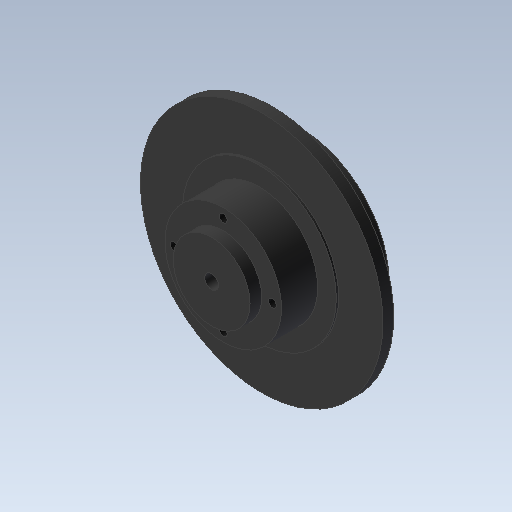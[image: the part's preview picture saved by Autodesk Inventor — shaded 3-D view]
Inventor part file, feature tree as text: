
AUTODESK INVENTOR PART (.ipt)
format: ipt  version: 2021 (Build 250183000, 183)  size: 157,696 bytes
history: native  units: mm
features: sketch x7, extrude x6, hole x1
ambient origin geometry x8: Origin, YZ Plane, XZ Plane, XY Plane, X Axis, Y Axis, Z Axis, Center Point
bodies: Solid1 (feature_tree)
feature tree (14):
  extrude  "Extrusion1"  Depth=6.0mm TaperAngle=0.0deg
  extrude  "Extrusion2"  Depth=2.3mm TaperAngle=0.0deg
  extrude  "Extrusion3"  Depth=0.5mm TaperAngle=0.0deg
  extrude  "Extrusion4"  Depth=7.75mm TaperAngle=0.0deg
  extrude  "Extrusion5"  Depth=2.5mm TaperAngle=0.0deg
  hole  "Hole1"  [1 undecoded]
  extrude  "Extrusion6"  Depth=5.0mm
  sketch  "Sketch1"  dims[d0=38.0mm d1=6.0mm d2=0.0mm]
  sketch  "Sketch2"  dims[d3=52.0mm d4=2.3mm d5=0.0mm]
  sketch  "Sketch3"  dims[d6=33.0mm d7=0.5mm d8=0.0mm]
  sketch  "Sketch4"  dims[d9=25.0mm d10=7.75mm d11=0.0mm]
  sketch  "Sketch5"  dims[d12=16.5mm d13=2.5mm d14=0.0mm]
  sketch  "Sketch6"  dims[d15=10.55mm d16=40.0mm d18=360.0deg]
  sketch  "Sketch7"  dims[d20=1.712861mm d21=4.4mm d22=4.0mm d23=2.0mm d24=90.0deg d25=5.0mm d26=0.0mm d27=3.0mm d28=0.0mm d29=0.0mm d30=0.75mm d31=0.375mm]
note: 1 required parameter value undecoded (feature->parameter linkage not recoverable at this tier; creation-order binding heuristic only, values carry confidence <= 0.55)
